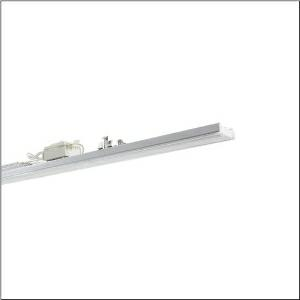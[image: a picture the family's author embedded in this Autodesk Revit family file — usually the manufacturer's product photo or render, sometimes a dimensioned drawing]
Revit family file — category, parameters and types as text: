
# Revit family: licross_11_recessed_mo_51tl12dn395g
name_source: partatom
category: Lighting Fixtures
units: mm (PartAtom-declared; Revit-internal decimal feet)

## family parameters
Cut with Voids When Loaded = No
Host = Face
Light Source = No
Part Type = Normal
Room Calculation Point = No
Round Connector Dimension = Use Diameter
Shared = No

## types (1)
- --- (1 x LED, 9840 lm, 56.7 W, 3000K)
    Apparent Load = 57 VA
    CIE Flux Codes = 67 92 99 100 100
    Color Rendering = 80
    Color Temperature = 3000K
    Default Elevation = 1800 mm
    Description = Licross 11 Recessed MO, luminaire insert, of sheet steel, coil coated, white, length: 1.500mm, width: 66mm, height: 67mm, LED rated luminous flux: 9.840lm, light colour: 830, SDCM (Standard Deviation of Colour Matching)MacAdam ≤ 2 SDCM (initial), control gear: DALI 2, with plug, 5-pole, with phase selection, mains connection: 220..240V, AC, 50/60Hz, rated input power: 57W, internal wiring halogen-free, primary optical cover: cover, of PMMA, light emission: direct distribution, primary light characteristic: symmetric, protection rating (complete): IP40, insulation class (complete): insulation class I (protective earthing), certification: CE, ENEC, VDE, UKCA, protection symbol: D if used in an environment without relevant dust loads with corresponding accessories, impact resistance: IK06, permissible ambient temperature for indoor applications: -25..+35°C, corresponds to IFS (International Featured Standards) requirements for safety and quality in the food industry, reducing of maximum allowable ambient temperature of 5°C with ceiling mounting, LABS conformity tested according to VDMA 24364:2018-05, The light source and the operating device comply with the requirements of the Ecodesign Regulation (EU) 2019/2020 and are replaceable in accordance with this regulation, packaging unit: 1 piece
    Height = 58 mm
    Lamp = 1 x LED
    Lamp Light Flux = 9840 lm
    Lamp Power = 56.7 W
    Lamp count = 1
    Length = 1500 mm
    Luminous efficacy = 174 lm/W
    Manufacturer = Siteco
    ModVariant = No
    Model = 51TL12DN395G
    Mounting Place = Ceiling
    Mounting Type = Pendant
    Number of Poles = 1
    OnlyDefault = Yes
    Power Factor = 1
    Product Name = Licross 11 Recessed MO
    Product group = luminaire insert | ceiling pendant
    ProductGroupID = 901
    Protection Class = Protection class I
    Protection Degree = IP 40
    RLX_Detail_Level = 1
    RLX_Emergency_Light_Flux = 0 lm
    RLX_Emergency_Type = 0
    RLX_Emergency_Type_DB = No
    RlxData = <blob elided: 24657 chars, md5=e974a5e1>
    Socket = socket
    Standby Power = 0 W
    System Light Flux = 9840 lm
    System Power = 57 W
    Type Comments = factory setting: luminous flux: 100 % | dim-lin: 254 | 378 mA
    Type Image = l_1296930.jpg
    URL = http://relux.com
    VarID = @adj_075581
    Voltage = 0 V
    Weight = 0.00 kg
    Width = 66 mm

## geometry (parser evidence)
native form markers: Blend x4, Sweep x9
no freeform markers — native parametric forms only
